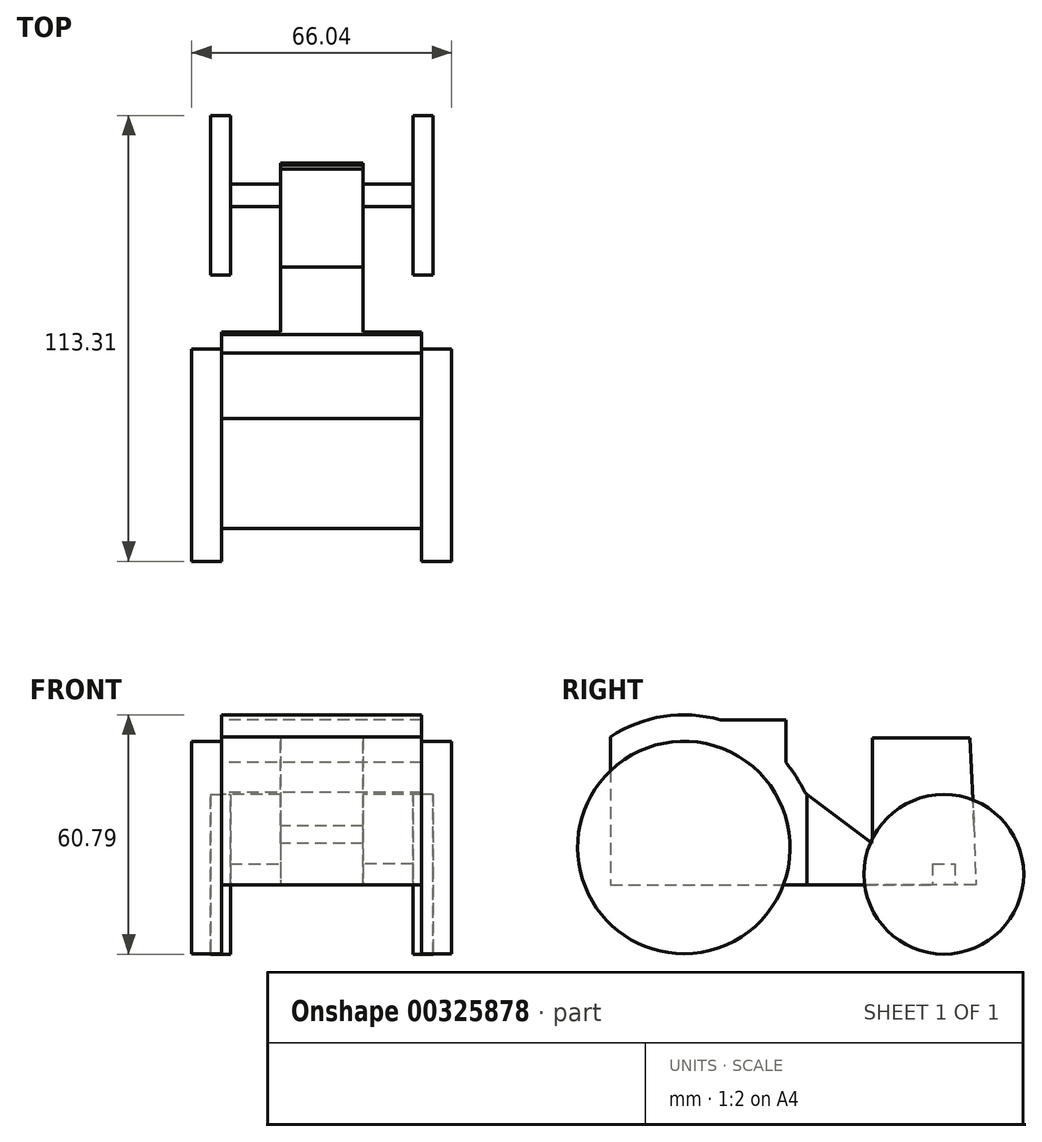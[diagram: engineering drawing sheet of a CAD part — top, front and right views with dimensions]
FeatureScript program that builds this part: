
annotation { "Feature Type Name" : "Feature", "Feature Type Description" : "" }
export const myFeature = defineFeature(function(context is Context, id is Id, definition is map)
    precondition{}
    {
        {
            var Q0;
            Q0=qCreatedBy(makeId("Right.planeOp"),FACE);
            var sketch = newSketch(context, id + "F0", { "sketchPlane" : qUnion([Q0])});
            skArc(sketch, "E0", {"start": v(-17.15, 12.93) * mm, "mid": v(-19.3, 16.92) * mm, "end": v(-21.96, 20.59) * mm});
            skLineSegment(sketch, "E1", {"start": v(-17.15, 12.93) * mm, "end": v(0, 0) * mm});
            skLineSegment(sketch, "E2", {"start": v(-38.55, 31.39) * mm, "end": v(-21.96, 31.39) * mm});
            skLineSegment(sketch, "E3", {"start": v(-21.96, 31.39) * mm, "end": v(-21.96, 20.59) * mm});
            skLineSegment(sketch, "E4", {"start": v(0, 0) * mm, "end": v(0, 26.77) * mm});
            skLineSegment(sketch, "E5", {"start": v(0, 26.77) * mm, "end": v(24.82, 26.77) * mm});
            skLineSegment(sketch, "E6", {"start": v(24.82, 26.77) * mm, "end": v(25.87, 4.51) * mm});
            skLineSegment(sketch, "E7", {"start": v(-66.47, 27.07) * mm, "end": v(-66.47, -10.53) * mm});
            skLineSegment(sketch, "E8", {"start": v(-66.47, -10.53) * mm, "end": v(26.32, -10.53) * mm});
            skLineSegment(sketch, "E9", {"start": v(25.87, 4.51) * mm, "end": v(26.32, -10.53) * mm});
            skArc(sketch, "E10.trimOffspring", {"start": v(-38.55, 31.39) * mm, "mid": v(-52.98, 32.3) * mm, "end": v(-66.47, 27.07) * mm});
            skSolve(sketch);
        }
        {
            var Q0;
            Q0 = qSketchRegion(id + "F0", true);
            extrude(context, id + "F1", {"entities" : qUnion([Q0]), "depth" : 50.8 * mm});
        }
        {
            var Q0;
            Q0=qCreatedBy(makeId("Top.planeOp"),FACE);
            var sketch = newSketch(context, id + "F2", { "sketchPlane" : qUnion([Q0])});
            skLineSegment(sketch, "E11.bottom", {"start": v(0, 37.3) * mm, "end": v(14.92, 37.3) * mm});
            skLineSegment(sketch, "E11.top", {"start": v(0, -16.54) * mm, "end": v(14.92, -16.54) * mm});
            skLineSegment(sketch, "E11.left", {"start": v(0, 37.3) * mm, "end": v(0, -16.54) * mm});
            skLineSegment(sketch, "E11.right", {"start": v(14.92, 37.3) * mm, "end": v(14.92, -16.54) * mm});
            skLineSegment(sketch, "E12.bottom", {"start": v(35.88, -16.54) * mm, "end": v(50.8, -16.54) * mm});
            skLineSegment(sketch, "E12.top", {"start": v(35.88, 37.3) * mm, "end": v(50.8, 37.3) * mm});
            skLineSegment(sketch, "E12.left", {"start": v(35.88, -16.54) * mm, "end": v(35.88, 37.3) * mm});
            skLineSegment(sketch, "E12.right", {"start": v(50.8, -16.54) * mm, "end": v(50.8, 37.3) * mm});
            skSolve(sketch);
        }
        {
            var Q0;
            Q0 = qSketchRegion(id + "F2", true);
            extrude(context, id + "F3", {"entities" : qUnion([Q0]), "operationType" : NewBodyOperationType.REMOVE, "endBound" : BoundingType.THROUGH_ALL, "depth" : 25.4 * mm});
        }
        {
            var Q0;
            Q0 = qSketchRegion(id + "F2", true);
            extrude(context, id + "F4", {"entities" : qUnion([Q0]), "operationType" : NewBodyOperationType.REMOVE, "endBound" : BoundingType.THROUGH_ALL, "oppositeDirection" : true, "depth" : 25.4 * mm});
        }
        {
            var Q0;
            Q0=makeQuery(id+"F1.opExtrude","CAP_FACE",FACE,{"disambiguationData":[OSD([sQuery(id+"F0.wireOp",EDGE,"E0"),sQuery(id+"F0.wireOp",EDGE,"E1"),sQuery(id+"F0.wireOp",EDGE,"E2"),sQuery(id+"F0.wireOp",EDGE,"E3"),sQuery(id+"F0.wireOp",EDGE,"E4"),sQuery(id+"F0.wireOp",EDGE,"E5"),sQuery(id+"F0.wireOp",EDGE,"E6"),sQuery(id+"F0.wireOp",EDGE,"E7"),sQuery(id+"F0.wireOp",EDGE,"E8"),sQuery(id+"F0.wireOp",EDGE,"E9"),sQuery(id+"F0.wireOp",EDGE,"E10.trimOffspring")])],"isStart":false});
            var sketch = newSketch(context, id + "F5", { "sketchPlane" : qUnion([Q0])});
            skCircle(sketch, "E13", {"center": v(-47.83, -1.02) * mm, "radius": 27 * mm});
            skSolve(sketch);
        }
        {
            var Q0;
            Q0 = qSketchRegion(id + "F5", true);
            extrude(context, id + "F6", {"entities" : qUnion([Q0]), "operationType" : NewBodyOperationType.ADD, "depth" : 7.62 * mm});
        }
        {
            var Q0;
            Q0=makeQuery(id+"F1.opExtrude","CAP_FACE",FACE,{"disambiguationData":[OSD([sQuery(id+"F0.wireOp",EDGE,"E0"),sQuery(id+"F0.wireOp",EDGE,"E1"),sQuery(id+"F0.wireOp",EDGE,"E2"),sQuery(id+"F0.wireOp",EDGE,"E3"),sQuery(id+"F0.wireOp",EDGE,"E4"),sQuery(id+"F0.wireOp",EDGE,"E5"),sQuery(id+"F0.wireOp",EDGE,"E6"),sQuery(id+"F0.wireOp",EDGE,"E7"),sQuery(id+"F0.wireOp",EDGE,"E8"),sQuery(id+"F0.wireOp",EDGE,"E9"),sQuery(id+"F0.wireOp",EDGE,"E10.trimOffspring")])],"isStart":true});
            var sketch = newSketch(context, id + "F7", { "sketchPlane" : qUnion([Q0])});
            skCircle(sketch, "E14", {"center": v(47.83, -1.02) * mm, "radius": 27 * mm});
            skSolve(sketch);
        }
        {
            var Q0;
            Q0 = qSketchRegion(id + "F7", true);
            extrude(context, id + "F8", {"entities" : qUnion([Q0]), "operationType" : NewBodyOperationType.ADD, "depth" : 7.62 * mm});
        }
        {
            var Q0;
            {var subQ0=sQuery(id+"F2.wireOp",EDGE,"E12.left");var subQ2=sQuery(id+"F2.wireOp",EDGE,"E12.bottom");var subQ5=makeQuery(id+"F3.opExtrude","SWEPT_FACE",FACE,{"disambiguationData":[OSD([subQ0])]});Q0=makeQuery(id+"F4.boolean.opBoolean","MERGE",FACE,{"derivedFrom":[makeQuery(id+"F3.boolean.opBoolean","COPY",FACE,{"disambiguationData":[TD([makeQuery(id+"F3.opExtrude","SWEPT_FACE",FACE,{"disambiguationData":[OSD([subQ2])]})])],"derivedFrom":subQ5}),makeQuery(id+"F3.boolean.opBoolean","COPY",FACE,{"disambiguationData":[TD([makeQuery(id+"F1.opExtrude","SWEPT_FACE",FACE,{"disambiguationData":[OSD([sQuery(id+"F0.wireOp",EDGE,"E5")])]})])],"derivedFrom":subQ5}),makeQuery(id+"F4.opExtrude","SWEPT_FACE",FACE,{"disambiguationData":[OSD([subQ0])]})]});}
            var sketch = newSketch(context, id + "F9", { "sketchPlane" : qUnion([Q0])});
            skLineSegment(sketch, "E15.bottom", {"start": v(15.34, -5.11) * mm, "end": v(21.06, -5.11) * mm});
            skLineSegment(sketch, "E15.top", {"start": v(15.34, -10.53) * mm, "end": v(21.06, -10.53) * mm});
            skLineSegment(sketch, "E15.left", {"start": v(15.34, -5.11) * mm, "end": v(15.34, -10.53) * mm});
            skLineSegment(sketch, "E15.right", {"start": v(21.06, -5.11) * mm, "end": v(21.06, -10.53) * mm});
            skSolve(sketch);
        }
        {
            var Q0;
            Q0 = qSketchRegion(id + "F9", true);
            extrude(context, id + "F10", {"entities" : qUnion([Q0]), "operationType" : NewBodyOperationType.ADD, "depth" : 12.7 * mm});
        }
        {
            var Q0;
            {var subQ0=sQuery(id+"F2.wireOp",EDGE,"E11.right");var subQ2=makeQuery(id+"F3.opExtrude","SWEPT_FACE",FACE,{"disambiguationData":[OSD([subQ0])]});var subQ4=sQuery(id+"F2.wireOp",EDGE,"E11.top");Q0=makeQuery(id+"F4.boolean.opBoolean","MERGE",FACE,{"derivedFrom":[makeQuery(id+"F3.boolean.opBoolean","COPY",FACE,{"disambiguationData":[TD([makeQuery(id+"F3.opExtrude","SWEPT_FACE",FACE,{"disambiguationData":[OSD([subQ4])]})])],"derivedFrom":subQ2}),makeQuery(id+"F3.boolean.opBoolean","COPY",FACE,{"disambiguationData":[TD([makeQuery(id+"F1.opExtrude","SWEPT_FACE",FACE,{"disambiguationData":[OSD([sQuery(id+"F0.wireOp",EDGE,"E5")])]})])],"derivedFrom":subQ2}),makeQuery(id+"F4.opExtrude","SWEPT_FACE",FACE,{"disambiguationData":[OSD([subQ0])]})]});}
            var sketch = newSketch(context, id + "F11", { "sketchPlane" : qUnion([Q0])});
            skLineSegment(sketch, "E16.bottom", {"start": v(-21.06, -5.11) * mm, "end": v(-15.34, -5.11) * mm});
            skLineSegment(sketch, "E16.top", {"start": v(-21.06, -10.53) * mm, "end": v(-15.34, -10.53) * mm});
            skLineSegment(sketch, "E16.left", {"start": v(-21.06, -5.11) * mm, "end": v(-21.06, -10.53) * mm});
            skLineSegment(sketch, "E16.right", {"start": v(-15.34, -5.11) * mm, "end": v(-15.34, -10.53) * mm});
            skSolve(sketch);
        }
        {
            var Q0;
            Q0 = qSketchRegion(id + "F11", true);
            extrude(context, id + "F12", {"entities" : qUnion([Q0]), "operationType" : NewBodyOperationType.ADD, "depth" : 12.7 * mm});
        }
        {
            var Q0;
            Q0=makeQuery(id+"F12.opExtrude","CAP_FACE",FACE,{"disambiguationData":[OSD([sQuery(id+"F11.wireOp",EDGE,"E16.bottom"),sQuery(id+"F11.wireOp",EDGE,"E16.top"),sQuery(id+"F11.wireOp",EDGE,"E16.left"),sQuery(id+"F11.wireOp",EDGE,"E16.right")])],"isStart":false});
            var sketch = newSketch(context, id + "F13", { "sketchPlane" : qUnion([Q0])});
            skCircle(sketch, "E17", {"center": v(-18.2, -7.82) * mm, "radius": 20.28 * mm});
            skPoint(sketch, "E18", {"position": v(-21.06, -7.82) * mm});
            skPoint(sketch, "E19", {"position": v(-18.2, -10.53) * mm});
            skLineSegment(sketch, "E20", {"start": v(76.62, -28.01) * mm, "end": v(-44.14, -28.01) * mm, "construction": true});
            skSolve(sketch);
        }
        {
            var Q0;
            Q0 = qSketchRegion(id + "F13", true);
            extrude(context, id + "F14", {"entities" : qUnion([Q0]), "depth" : 5.08 * mm});
        }
        {
            var Q0;
            Q0=makeQuery(id+"F10.opExtrude","CAP_FACE",FACE,{"disambiguationData":[OSD([sQuery(id+"F9.wireOp",EDGE,"E15.bottom"),sQuery(id+"F9.wireOp",EDGE,"E15.top"),sQuery(id+"F9.wireOp",EDGE,"E15.left"),sQuery(id+"F9.wireOp",EDGE,"E15.right")])],"isStart":false});
            var sketch = newSketch(context, id + "F15", { "sketchPlane" : qUnion([Q0])});
            skCircle(sketch, "E21", {"center": v(18.2, -7.82) * mm, "radius": 20.28 * mm});
            skSolve(sketch);
        }
        {
            var Q0;
            Q0 = qSketchRegion(id + "F15", true);
            extrude(context, id + "F16", {"entities" : qUnion([Q0]), "operationType" : NewBodyOperationType.ADD, "depth" : 5.08 * mm});
        }
    });
